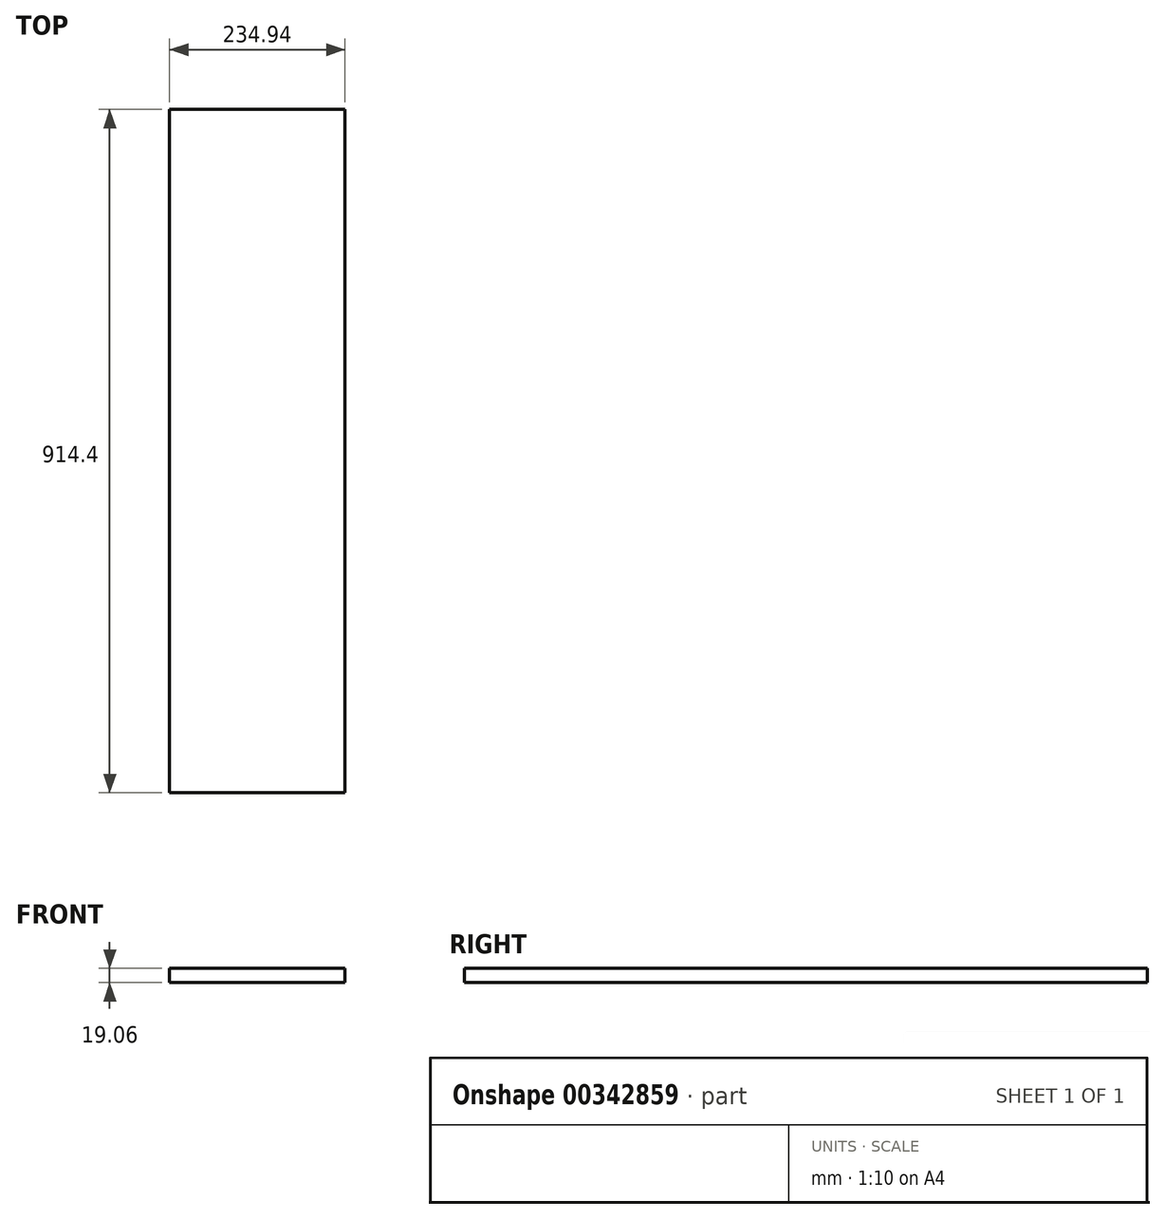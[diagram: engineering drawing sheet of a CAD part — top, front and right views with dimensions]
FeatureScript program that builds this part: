
annotation { "Feature Type Name" : "Feature", "Feature Type Description" : "" }
export const myFeature = defineFeature(function(context is Context, id is Id, definition is map)
    precondition{}
    {
        {
            var Q0;
            Q0=qCreatedBy(makeId("Front.planeOp"),FACE);
            var sketch = newSketch(context, id + "F0", { "sketchPlane" : qUnion([Q0])});
            skLineSegment(sketch, "E0.bottom", {"start": v(117.48, 9.53) * mm, "end": v(-117.48, 9.53) * mm});
            skLineSegment(sketch, "E0.top", {"start": v(117.48, -9.52) * mm, "end": v(-117.48, -9.52) * mm});
            skLineSegment(sketch, "E0.left", {"start": v(117.48, 9.53) * mm, "end": v(117.48, -9.52) * mm});
            skLineSegment(sketch, "E0.right", {"start": v(-117.48, 9.53) * mm, "end": v(-117.48, -9.52) * mm});
            skPoint(sketch, "E0.middle", {"position": v(0, 0) * mm});
            skSolve(sketch);
        }
        {
            var Q0;
            Q0=makeQuery(id+"F0.imprint","IMPRINT",FACE,{"disambiguationData":[TD([[makeQuery(id+"F0.imprint","IMPRINT",EDGE,{"derivedFrom":sQuery(id+"F0.wireOp",EDGE,"E0.bottom")}),1.0]])]});
            extrude(context, id + "F1", {"entities" : qUnion([Q0]), "endBound" : BoundingType.SYMMETRIC, "depth" : 914.4 * mm});
        }
    });
